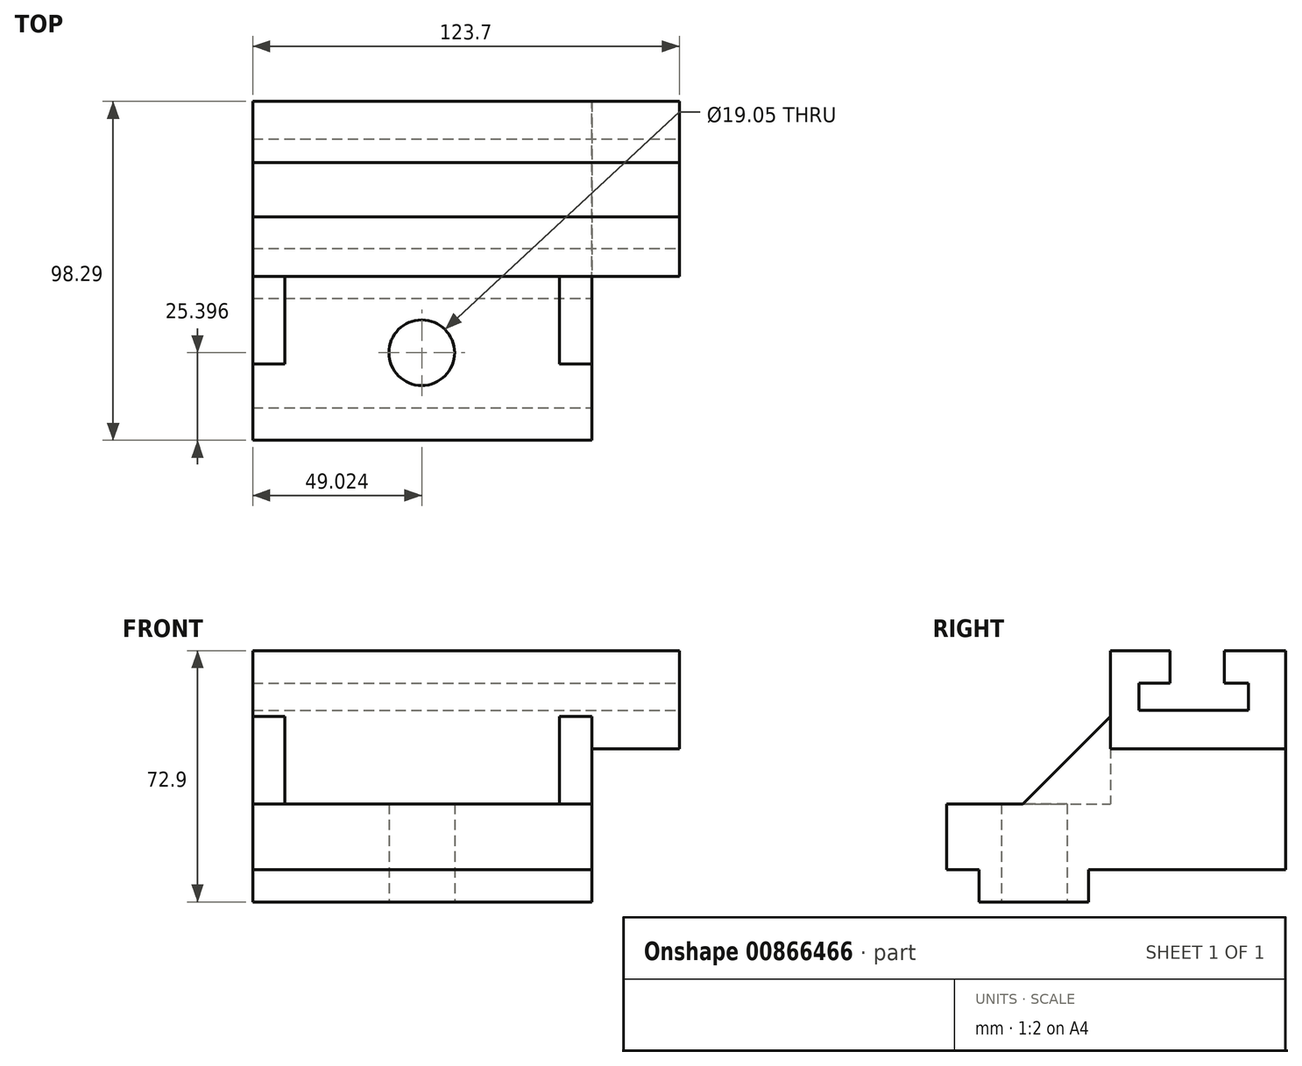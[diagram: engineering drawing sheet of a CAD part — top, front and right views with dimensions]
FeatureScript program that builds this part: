
annotation { "Feature Type Name" : "Feature", "Feature Type Description" : "" }
export const myFeature = defineFeature(function(context is Context, id is Id, definition is map)
    precondition{}
    {
        {
            var Q0;
            Q0=qCreatedBy(makeId("Top.planeOp"),FACE);
            var sketch = newSketch(context, id + "F0", { "sketchPlane" : qUnion([Q0])});
            skLineSegment(sketch, "E0.bottom", {"start": v(-41.55, 59.4) * mm, "end": v(82.15, 59.4) * mm});
            skLineSegment(sketch, "E0.top", {"start": v(-41.55, 8.6) * mm, "end": v(82.15, 8.6) * mm});
            skLineSegment(sketch, "E0.left", {"start": v(-41.55, 59.4) * mm, "end": v(-41.55, 8.6) * mm});
            skLineSegment(sketch, "E0.right", {"start": v(82.15, 59.4) * mm, "end": v(82.15, 8.6) * mm});
            skLineSegment(sketch, "E1.bottom", {"start": v(-41.55, 8.6) * mm, "end": v(56.75, 8.6) * mm});
            skLineSegment(sketch, "E1.top", {"start": v(-41.55, -38.9) * mm, "end": v(56.75, -38.9) * mm});
            skLineSegment(sketch, "E1.left", {"start": v(-41.55, 8.6) * mm, "end": v(-41.55, -38.9) * mm});
            skLineSegment(sketch, "E1.right", {"start": v(56.75, 8.6) * mm, "end": v(56.75, -38.9) * mm});
            skLineSegment(sketch, "E2", {"start": v(-32.15, 8.6) * mm, "end": v(-32.15, -16.8) * mm});
            skLineSegment(sketch, "E3", {"start": v(-32.15, -16.8) * mm, "end": v(-41.55, -16.8) * mm});
            skLineSegment(sketch, "E4", {"start": v(47.35, 8.6) * mm, "end": v(47.35, -16.8) * mm});
            skLineSegment(sketch, "E5", {"start": v(47.35, -16.8) * mm, "end": v(56.75, -16.8) * mm});
            skLineSegment(sketch, "E6", {"start": v(-41.55, 25.88) * mm, "end": v(82.15, 25.88) * mm});
            skLineSegment(sketch, "E7", {"start": v(-41.55, 41.62) * mm, "end": v(82.15, 41.62) * mm});
            skCircle(sketch, "E8", {"center": v(7.47, -13.5) * mm, "radius": 9.53 * mm});
            skSolve(sketch);
        }
        {
            var Q0;
            {var subQ8=sQuery(id+"F0.wireOp",EDGE,"E6");Q0=makeQuery(id+"F0.imprint","IMPRINT",FACE,{"disambiguationData":[TD([[makeQuery(id+"F0.imprint","IMPRINT",EDGE,{"derivedFrom":subQ8}),-1.0]])]});}
            var Q1;
            {var subQ0=sQuery(id+"F0.wireOp",EDGE,"E6");Q1=makeQuery(id+"F0.imprint","IMPRINT",FACE,{"disambiguationData":[TD([[makeQuery(id+"F0.imprint","IMPRINT",EDGE,{"derivedFrom":subQ0}),1.0]])]});}
            var Q2;
            {var subQ0=sQuery(id+"F0.wireOp",EDGE,"E0.bottom");Q2=makeQuery(id+"F0.imprint","IMPRINT",FACE,{"disambiguationData":[TD([[makeQuery(id+"F0.imprint","IMPRINT",EDGE,{"derivedFrom":subQ0}),-1.0]])]});}
            extrude(context, id + "F1", {"entities" : qUnion([Q0, Q1, Q2]), "depth" : 72.9 * mm, "offsetDistance" : 25.4 * mm});
        }
        {
            var Q0;
            {var subQ1=sQuery(id+"F0.wireOp",EDGE,"E1.top");Q0=makeQuery(id+"F0.imprint","IMPRINT",FACE,{"disambiguationData":[TD([[makeQuery(id+"F0.imprint","IMPRINT",EDGE,{"derivedFrom":subQ1}),1.0]])]});}
            var Q1;
            {var subQ3=sQuery(id+"F0.wireOp",EDGE,"E4");Q1=makeQuery(id+"F0.imprint","IMPRINT",FACE,{"disambiguationData":[TD([[makeQuery(id+"F0.imprint","IMPRINT",EDGE,{"derivedFrom":subQ3}),1.0]])]});}
            var Q2;
            {var subQ0=sQuery(id+"F0.wireOp",EDGE,"E2");Q2=makeQuery(id+"F0.imprint","IMPRINT",FACE,{"disambiguationData":[TD([[makeQuery(id+"F0.imprint","IMPRINT",EDGE,{"derivedFrom":subQ0}),-1.0]])]});}
            extrude(context, id + "F2", {"entities" : qUnion([Q0, Q1, Q2]), "operationType" : NewBodyOperationType.ADD, "depth" : 28.45 * mm, "offsetDistance" : 25.4 * mm});
        }
        {
            var Q0;
            {var subQ3=sQuery(id+"F0.wireOp",EDGE,"E4");Q0=makeQuery(id+"F0.imprint","IMPRINT",FACE,{"disambiguationData":[TD([[makeQuery(id+"F0.imprint","IMPRINT",EDGE,{"derivedFrom":subQ3}),1.0]])]});}
            var Q1;
            {var subQ0=sQuery(id+"F0.wireOp",EDGE,"E2");Q1=makeQuery(id+"F0.imprint","IMPRINT",FACE,{"disambiguationData":[TD([[makeQuery(id+"F0.imprint","IMPRINT",EDGE,{"derivedFrom":subQ0}),-1.0]])]});}
            extrude(context, id + "F3", {"entities" : qUnion([Q0, Q1]), "operationType" : NewBodyOperationType.ADD, "depth" : 53.85 * mm, "offsetDistance" : 25.4 * mm});
        }
        {
            var Q0;
            {var subQ0=sQuery(id+"F0.wireOp",EDGE,"E1.right");Q0=makeQuery(id+"F3.boolean.opBoolean","MERGE",FACE,{"derivedFrom":[makeQuery(id+"F2.opExtrude","SWEPT_FACE",FACE,{"disambiguationData":[OSD([subQ0])]}),makeQuery(id+"F3.opExtrude","SWEPT_FACE",FACE,{"disambiguationData":[OSD([subQ0])]})]});}
            var sketch = newSketch(context, id + "F4", { "sketchPlane" : qUnion([Q0])});
            skLineSegment(sketch, "E9", {"start": v(-38.9, 9.4) * mm, "end": v(-29.5, 9.4) * mm});
            skLineSegment(sketch, "E10", {"start": v(-29.5, 9.4) * mm, "end": v(-29.5, 0) * mm});
            skLineSegment(sketch, "E11", {"start": v(2.25, 0) * mm, "end": v(2.25, 9.4) * mm});
            skLineSegment(sketch, "E12", {"start": v(2.25, 9.4) * mm, "end": v(8.6, 9.4) * mm});
            skSolve(sketch);
        }
        {
            var Q0;
            Q0=makeQuery(id+"F1.opExtrude","SWEPT_FACE",FACE,{"disambiguationData":[OSD([sQuery(id+"F0.wireOp",EDGE,"E0.right")])]});
            var sketch = newSketch(context, id + "F5", { "sketchPlane" : qUnion([Q0])});
            skLineSegment(sketch, "E13", {"start": v(8.6, 40.2) * mm, "end": v(59.4, 40.2) * mm});
            skSolve(sketch);
        }
        {
            var Q0;
            Q0=makeQuery(id+"F1.opExtrude","SWEPT_FACE",FACE,{"disambiguationData":[OSD([sQuery(id+"F0.wireOp",EDGE,"E0.top")])]});
            var sketch = newSketch(context, id + "F6", { "sketchPlane" : qUnion([Q0])});
            skLineSegment(sketch, "E14", {"start": v(82.15, 44.45) * mm, "end": v(56.75, 44.45) * mm});
            skSolve(sketch);
        }
        {
            var Q0;
            {var subQ0=sQuery(id+"F5.wireOp",EDGE,"E13");Q0=makeQuery(id+"F5.imprint","IMPRINT",FACE,{"disambiguationData":[TD([[makeQuery(id+"F5.imprint","IMPRINT",EDGE,{"derivedFrom":subQ0}),-1.0]])]});}
            extrude(context, id + "F7", {"entities" : qUnion([Q0]), "operationType" : NewBodyOperationType.REMOVE, "oppositeDirection" : true, "depth" : 25.4 * mm, "offsetDistance" : 25.4 * mm});
        }
        {
            var Q0;
            {var subQ0=sQuery(id+"F4.wireOp",EDGE,"E9");Q0=makeQuery(id+"F4.imprint","IMPRINT",FACE,{"disambiguationData":[TD([[makeQuery(id+"F4.imprint","IMPRINT",EDGE,{"derivedFrom":subQ0}),-1.0]])]});}
            extrude(context, id + "F8", {"entities" : qUnion([Q0]), "operationType" : NewBodyOperationType.REMOVE, "oppositeDirection" : true, "depth" : 111 * mm, "offsetDistance" : 25.4 * mm});
        }
        {
            var Q0;
            {var subQ0=sQuery(id+"F0.wireOp",EDGE,"E1.right");Q0=makeQuery(id+"F7.boolean.opBoolean","MERGE",FACE,{"derivedFrom":[makeQuery(id+"F3.boolean.opBoolean","MERGE",FACE,{"derivedFrom":[makeQuery(id+"F2.opExtrude","SWEPT_FACE",FACE,{"disambiguationData":[OSD([subQ0])]}),makeQuery(id+"F3.opExtrude","SWEPT_FACE",FACE,{"disambiguationData":[OSD([subQ0])]})]})],"fromTools":[makeQuery(id+"F7.opExtrude","CAP_FACE",FACE,{"disambiguationData":[OSD([sQuery(id+"F0.wireOp",EDGE,"E0.bottom"),sQuery(id+"F0.wireOp",EDGE,"E0.top"),sQuery(id+"F0.wireOp",EDGE,"E0.right"),sQuery(id+"F5.wireOp",EDGE,"E13")])],"isStart":false})]});}
            var sketch = newSketch(context, id + "F9", { "sketchPlane" : qUnion([Q0])});
            skLineSegment(sketch, "E15", {"start": v(2.25, 0) * mm, "end": v(2.25, 9.4) * mm});
            skLineSegment(sketch, "E16", {"start": v(2.25, 9.4) * mm, "end": v(59.4, 9.4) * mm});
            skSolve(sketch);
        }
        {
            var Q0;
            {var subQ0=sQuery(id+"F9.wireOp",EDGE,"E15");Q0=makeQuery(id+"F9.imprint","IMPRINT",FACE,{"disambiguationData":[TD([[makeQuery(id+"F9.imprint","IMPRINT",EDGE,{"derivedFrom":subQ0}),-1.0]])]});}
            extrude(context, id + "F10", {"entities" : qUnion([Q0]), "operationType" : NewBodyOperationType.REMOVE, "oppositeDirection" : true, "depth" : 120.4 * mm, "offsetDistance" : 25.4 * mm});
        }
        {
            var Q0;
            Q0=makeQuery(id+"F3.opExtrude","SWEPT_FACE",FACE,{"disambiguationData":[OSD([sQuery(id+"F0.wireOp",EDGE,"E2")])]});
            var sketch = newSketch(context, id + "F11", { "sketchPlane" : qUnion([Q0])});
            skLineSegment(sketch, "E17", {"start": v(-16.8, 28.45) * mm, "end": v(8.6, 53.85) * mm});
            skSolve(sketch);
        }
        {
            var Q0;
            Q0=makeQuery(id+"F11.imprint","IMPRINT",FACE,{"disambiguationData":[TD([[makeQuery(id+"F11.imprint","IMPRINT",EDGE,{"derivedFrom":sQuery(id+"F11.wireOp",EDGE,"E17")}),1.0]])]});
            extrude(context, id + "F12", {"entities" : qUnion([Q0]), "operationType" : NewBodyOperationType.REMOVE, "oppositeDirection" : true, "depth" : 25.4 * mm, "offsetDistance" : 25.4 * mm});
        }
        {
            var Q0;
            Q0=makeQuery(id+"F3.opExtrude","SWEPT_FACE",FACE,{"disambiguationData":[OSD([sQuery(id+"F0.wireOp",EDGE,"E4")])]});
            var sketch = newSketch(context, id + "F13", { "sketchPlane" : qUnion([Q0])});
            skLineSegment(sketch, "E18", {"start": v(-8.6, 53.85) * mm, "end": v(16.8, 28.45) * mm});
            skSolve(sketch);
        }
        {
            var Q0;
            Q0 = qSketchRegion(id + "F13", true);
            var Q1;
            Q1=makeQuery(id+"F13.imprint","IMPRINT",FACE,{"disambiguationData":[TD([[makeQuery(id+"F13.imprint","IMPRINT",EDGE,{"derivedFrom":sQuery(id+"F13.wireOp",EDGE,"E18")}),1.0]])]});
            extrude(context, id + "F14", {"entities" : qUnion([Q0, Q1]), "operationType" : NewBodyOperationType.REMOVE, "oppositeDirection" : true, "depth" : 25.4 * mm, "offsetDistance" : 25.4 * mm});
        }
        {
            var Q0;
            Q0=makeQuery(id+"F1.opExtrude","SWEPT_FACE",FACE,{"disambiguationData":[OSD([sQuery(id+"F0.wireOp",EDGE,"E0.right")])]});
            var sketch = newSketch(context, id + "F15", { "sketchPlane" : qUnion([Q0])});
            skLineSegment(sketch, "E19", {"start": v(25.88, 72.9) * mm, "end": v(25.88, 63.5) * mm});
            skLineSegment(sketch, "E20", {"start": v(25.88, 63.5) * mm, "end": v(16.79, 63.5) * mm});
            skLineSegment(sketch, "E21", {"start": v(16.79, 63.5) * mm, "end": v(16.79, 55.63) * mm});
            skLineSegment(sketch, "E22", {"start": v(16.79, 55.63) * mm, "end": v(48.54, 55.63) * mm});
            skLineSegment(sketch, "E23", {"start": v(48.54, 55.63) * mm, "end": v(48.54, 63.5) * mm});
            skLineSegment(sketch, "E24", {"start": v(48.54, 63.5) * mm, "end": v(41.62, 63.5) * mm});
            skLineSegment(sketch, "E25", {"start": v(41.62, 63.5) * mm, "end": v(41.62, 72.9) * mm});
            skSolve(sketch);
        }
        {
            var Q0;
            {var subQ0=sQuery(id+"F6.wireOp",EDGE,"E14");Q0=makeQuery(id+"F6.imprint","IMPRINT",FACE,{"disambiguationData":[TD([[makeQuery(id+"F6.imprint","IMPRINT",EDGE,{"derivedFrom":subQ0}),1.0]])]});}
            extrude(context, id + "F16", {"entities" : qUnion([Q0]), "operationType" : NewBodyOperationType.REMOVE, "oppositeDirection" : true, "depth" : 65.53 * mm, "offsetDistance" : 25.4 * mm});
        }
        {
            var Q0;
            {var subQ0=sQuery(id+"F15.wireOp",EDGE,"E19");Q0=makeQuery(id+"F15.imprint","IMPRINT",FACE,{"disambiguationData":[TD([[makeQuery(id+"F15.imprint","IMPRINT",EDGE,{"derivedFrom":subQ0}),1.0]])]});}
            extrude(context, id + "F17", {"entities" : qUnion([Q0]), "operationType" : NewBodyOperationType.REMOVE, "oppositeDirection" : true, "depth" : 161.04 * mm, "offsetDistance" : 25.4 * mm});
        }
    });
